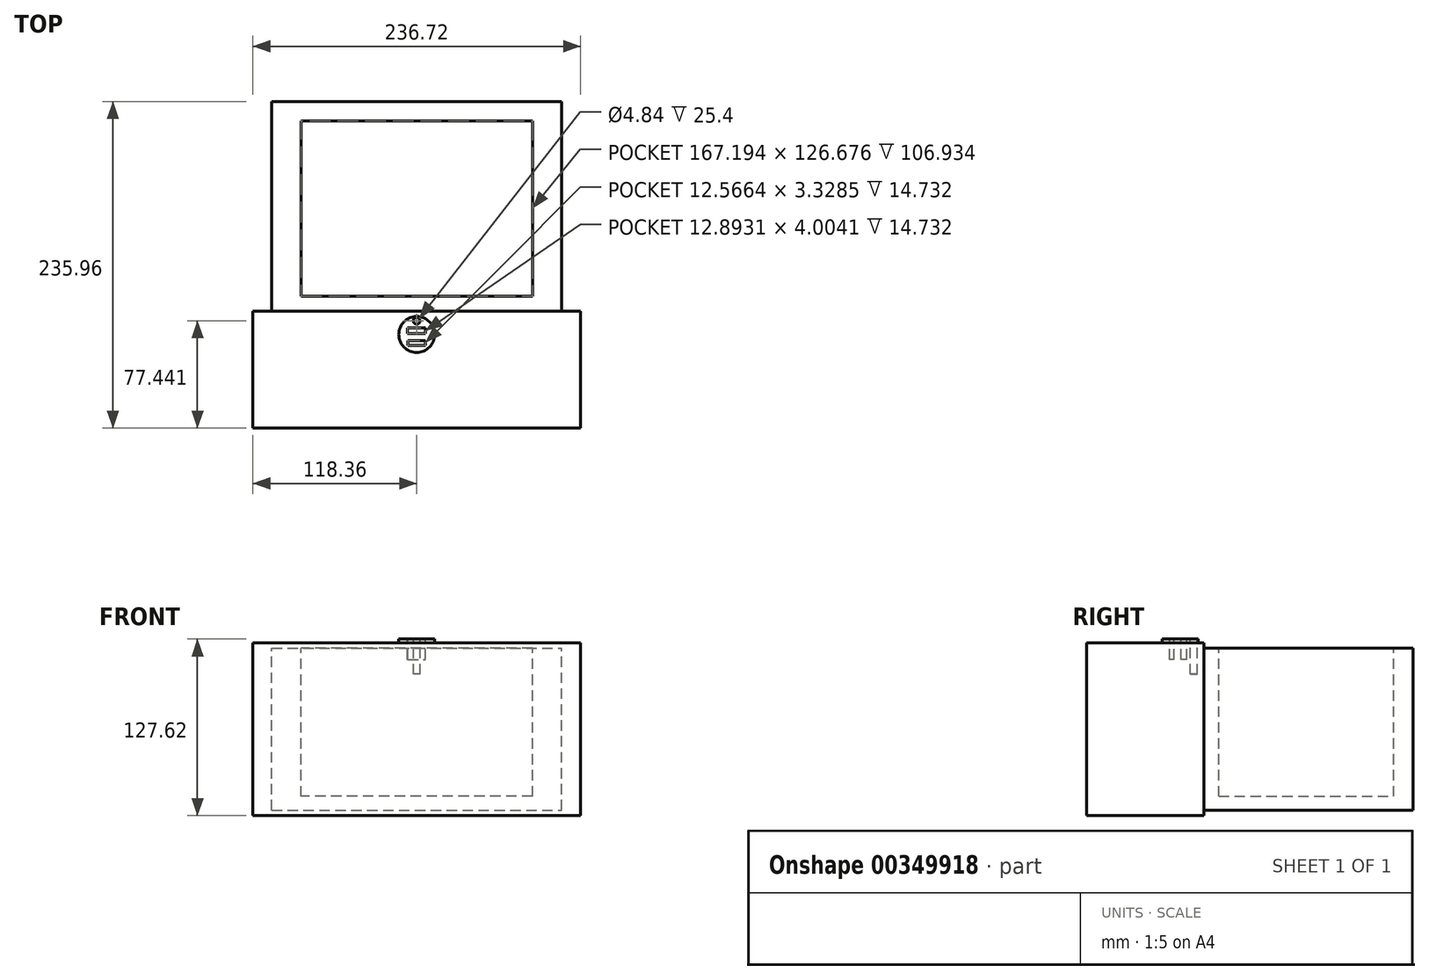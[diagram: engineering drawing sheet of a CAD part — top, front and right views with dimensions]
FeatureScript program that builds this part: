
annotation { "Feature Type Name" : "Feature", "Feature Type Description" : "" }
export const myFeature = defineFeature(function(context is Context, id is Id, definition is map)
    precondition{}
    {
        {
            var Q0;
            Q0=qCreatedBy(makeId("Front.planeOp"),FACE);
            var sketch = newSketch(context, id + "F0", { "sketchPlane" : qUnion([Q0])});
            skLineSegment(sketch, "E0.bottom", {"start": v(118.36, -62.41) * mm, "end": v(-118.36, -62.41) * mm});
            skLineSegment(sketch, "E0.top", {"start": v(118.36, 62.41) * mm, "end": v(-118.36, 62.41) * mm});
            skLineSegment(sketch, "E0.left", {"start": v(118.36, -62.41) * mm, "end": v(118.36, 62.41) * mm});
            skLineSegment(sketch, "E0.right", {"start": v(-118.36, -62.41) * mm, "end": v(-118.36, 62.41) * mm});
            skPoint(sketch, "E0.middle", {"position": v(0, 0) * mm});
            skSolve(sketch);
        }
        {
            var Q0;
            Q0 = qSketchRegion(id + "F0", true);
            extrude(context, id + "F1", {"entities" : qUnion([Q0]), "depth" : 84.58 * mm, "offsetDistance" : 25.4 * mm});
        }
        {
            var Q0;
            Q0=makeQuery(id+"F1.opExtrude","CAP_FACE",FACE,{"disambiguationData":[OSD([sQuery(id+"F0.wireOp",EDGE,"E0.bottom"),sQuery(id+"F0.wireOp",EDGE,"E0.top"),sQuery(id+"F0.wireOp",EDGE,"E0.left"),sQuery(id+"F0.wireOp",EDGE,"E0.right")])],"isStart":true});
            var sketch = newSketch(context, id + "F2", { "sketchPlane" : qUnion([Q0])});
            skLineSegment(sketch, "E1.bottom", {"start": v(104.83, -58.5) * mm, "end": v(-104.83, -58.5) * mm});
            skLineSegment(sketch, "E1.top", {"start": v(104.83, 58.5) * mm, "end": v(-104.83, 58.5) * mm});
            skLineSegment(sketch, "E1.left", {"start": v(104.83, -58.5) * mm, "end": v(104.83, 58.5) * mm});
            skLineSegment(sketch, "E1.right", {"start": v(-104.83, -58.5) * mm, "end": v(-104.83, 58.5) * mm});
            skPoint(sketch, "E1.middle", {"position": v(0, 0) * mm});
            skSolve(sketch);
        }
        {
            var Q0;
            Q0 = qSketchRegion(id + "F2", true);
            extrude(context, id + "F3", {"entities" : qUnion([Q0]), "operationType" : NewBodyOperationType.ADD, "depth" : 151.38 * mm, "offsetDistance" : 25.4 * mm});
        }
        {
            var Q0;
            Q0=makeQuery(id+"F3.opExtrude","SWEPT_FACE",FACE,{"disambiguationData":[OSD([sQuery(id+"F2.wireOp",EDGE,"E1.top")])]});
            var sketch = newSketch(context, id + "F4", { "sketchPlane" : qUnion([Q0])});
            skLineSegment(sketch, "E2.bottom", {"start": v(83.6, 10.81) * mm, "end": v(-83.6, 10.81) * mm});
            skLineSegment(sketch, "E2.top", {"start": v(83.6, 137.49) * mm, "end": v(-83.6, 137.49) * mm});
            skLineSegment(sketch, "E2.left", {"start": v(83.6, 10.81) * mm, "end": v(83.6, 137.49) * mm});
            skLineSegment(sketch, "E2.right", {"start": v(-83.6, 10.81) * mm, "end": v(-83.6, 137.49) * mm});
            skPoint(sketch, "E2.middle", {"position": v(0, 74.15) * mm});
            skSolve(sketch);
        }
        {
            var Q0;
            Q0 = qSketchRegion(id + "F4", true);
            extrude(context, id + "F5", {"entities" : qUnion([Q0]), "operationType" : NewBodyOperationType.REMOVE, "oppositeDirection" : true, "depth" : 106.93 * mm, "offsetDistance" : 25.4 * mm});
        }
        {
            var Q0;
            Q0=makeQuery(id+"F1.opExtrude","SWEPT_FACE",FACE,{"disambiguationData":[OSD([sQuery(id+"F0.wireOp",EDGE,"E0.top")])]});
            var sketch = newSketch(context, id + "F6", { "sketchPlane" : qUnion([Q0])});
            skCircle(sketch, "E3", {"center": v(0, -16.96) * mm, "radius": 12.93 * mm});
            skSolve(sketch);
        }
        {
            var Q0;
            Q0 = qSketchRegion(id + "F6", true);
            extrude(context, id + "F7", {"entities" : qUnion([Q0]), "operationType" : NewBodyOperationType.ADD, "depth" : 2.8 * mm, "offsetDistance" : 25.4 * mm});
        }
        {
            var Q0;
            Q0=makeQuery(id+"F7.opExtrude","CAP_FACE",FACE,{"disambiguationData":[OSD([sQuery(id+"F6.wireOp",EDGE,"E3")])],"isStart":false});
            var sketch = newSketch(context, id + "F8", { "sketchPlane" : qUnion([Q0])});
            skLineSegment(sketch, "E4.bottom", {"start": v(-6.75, -12.35) * mm, "end": v(6.15, -12.35) * mm});
            skLineSegment(sketch, "E4.top", {"start": v(-6.75, -16.35) * mm, "end": v(6.15, -16.35) * mm});
            skLineSegment(sketch, "E4.left", {"start": v(-6.75, -12.35) * mm, "end": v(-6.75, -16.35) * mm});
            skLineSegment(sketch, "E4.right", {"start": v(6.15, -12.35) * mm, "end": v(6.15, -16.35) * mm});
            skLineSegment(sketch, "E5.bottom", {"start": v(-6.42, -21.4) * mm, "end": v(6.15, -21.4) * mm});
            skLineSegment(sketch, "E5.top", {"start": v(-6.42, -24.74) * mm, "end": v(6.15, -24.74) * mm});
            skLineSegment(sketch, "E5.left", {"start": v(-6.42, -21.4) * mm, "end": v(-6.42, -24.74) * mm});
            skLineSegment(sketch, "E5.right", {"start": v(6.15, -21.4) * mm, "end": v(6.15, -24.74) * mm});
            skSolve(sketch);
        }
        {
            var Q0;
            Q0 = qSketchRegion(id + "F8", true);
            extrude(context, id + "F9", {"entities" : qUnion([Q0]), "operationType" : NewBodyOperationType.REMOVE, "oppositeDirection" : true, "depth" : 14.73 * mm, "offsetDistance" : 25.4 * mm});
        }
        {
            var Q0;
            Q0=makeQuery(id+"F7.opExtrude","CAP_FACE",FACE,{"disambiguationData":[OSD([sQuery(id+"F6.wireOp",EDGE,"E3")])],"isStart":false});
            var sketch = newSketch(context, id + "F10", { "sketchPlane" : qUnion([Q0])});
            skCircle(sketch, "E6", {"center": v(0, -7.14) * mm, "radius": 2.42 * mm});
            skSolve(sketch);
        }
        {
            var Q0;
            Q0 = qSketchRegion(id + "F10", true);
            extrude(context, id + "F11", {"entities" : qUnion([Q0]), "operationType" : NewBodyOperationType.REMOVE, "oppositeDirection" : true, "depth" : 25.4 * mm, "offsetDistance" : 25.4 * mm});
        }
    });
